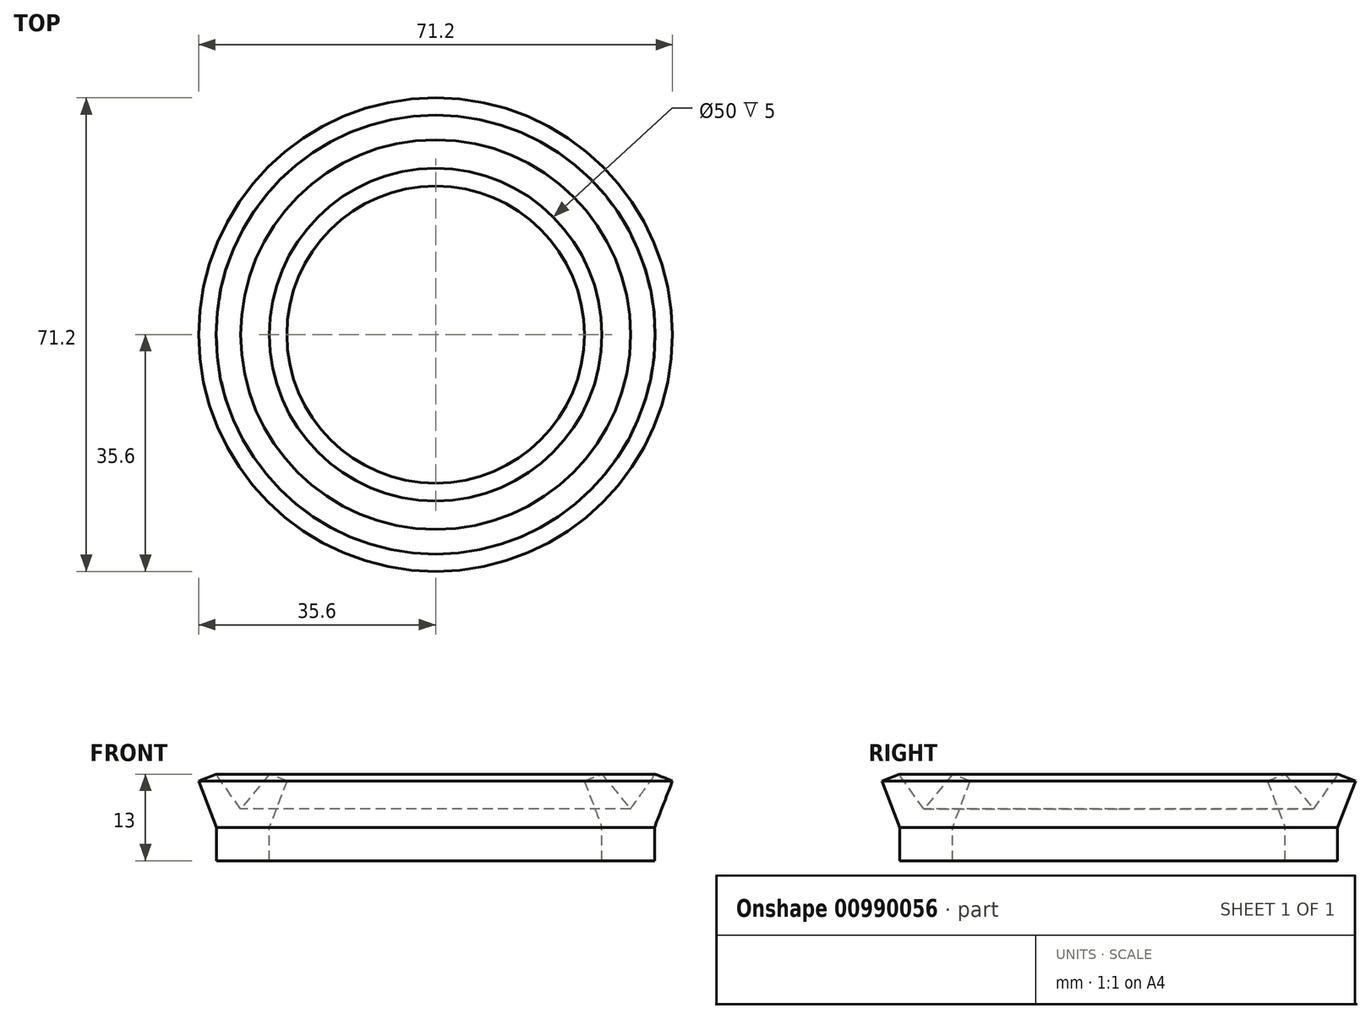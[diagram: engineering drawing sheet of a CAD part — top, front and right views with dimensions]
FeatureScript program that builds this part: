
annotation { "Feature Type Name" : "Feature", "Feature Type Description" : "" }
export const myFeature = defineFeature(function(context is Context, id is Id, definition is map)
    precondition{}
    {
        {
            var Q0;
            Q0=qCreatedBy(makeId("Front.planeOp"),FACE);
            var sketch = newSketch(context, id + "F0", { "sketchPlane" : qUnion([Q0])});
            skLineSegment(sketch, "E0", {"start": v(-32.9, 0) * mm, "end": v(-25, 0) * mm});
            skLineSegment(sketch, "E1", {"start": v(-25, 0) * mm, "end": v(-25, 5) * mm});
            skLineSegment(sketch, "E2", {"start": v(-25, 5) * mm, "end": v(-22.35, 12) * mm});
            skLineSegment(sketch, "E3", {"start": v(-22.35, 12) * mm, "end": v(-25, 13) * mm});
            skLineSegment(sketch, "E4", {"start": v(-32.9, 0) * mm, "end": v(-32.9, 5) * mm});
            skLineSegment(sketch, "E5", {"start": v(-35.6, 12) * mm, "end": v(-32.9, 5) * mm});
            skLineSegment(sketch, "E6", {"start": v(-35.6, 12) * mm, "end": v(-33, 13) * mm});
            skLineSegment(sketch, "E7", {"start": v(-33, 13) * mm, "end": v(-29.3, 7.78) * mm});
            skLineSegment(sketch, "E8", {"start": v(-29.3, 7.78) * mm, "end": v(-25, 13) * mm});
            skLineSegment(sketch, "E9", {"start": v(0, 32.35) * mm, "end": v(0, -17.54) * mm});
            skSolve(sketch);
        }
        {
            var Q0;
            Q0=makeQuery(id+"F0.imprint","IMPRINT",FACE,{"disambiguationData":[TD([[makeQuery(id+"F0.imprint","IMPRINT",EDGE,{"derivedFrom":sQuery(id+"F0.wireOp",EDGE,"E0")}),1.0]])]});
            var Q1;
            Q1=sQuery(id+"F0.wireOp",EDGE,"E9");
            revolve(context, id + "F1", {"surfaceOperationType" : NewSurfaceOperationType.NEW, "entities" : qUnion([Q0]), "axis" : qUnion([Q1]), "revolveType" : RevolveType.FULL});
        }
    });
